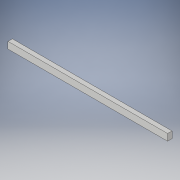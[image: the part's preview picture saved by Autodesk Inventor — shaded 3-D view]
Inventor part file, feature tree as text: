
AUTODESK INVENTOR PART (.ipt)
format: ipt  version: 2017 (Build 210142000, 142)  size: 92,160 bytes
history: native  units: in
note: dims shown in document units (in); Inventor stores cm internally (conversion verified against a paired STEP export)
features: extrude x1, sketch x1
ambient origin geometry x8: Origin, YZ Plane, XZ Plane, XY Plane, X Axis, Y Axis, Z Axis, Center Point
bodies: Solid1 (feature_tree)
feature tree (2):
  extrude  "Extrusion1"  Depth=3.0in
  sketch  "Sketch1"  dims[d0=72.0in d1=3.0in d2=2.0in d3=0.0in]
